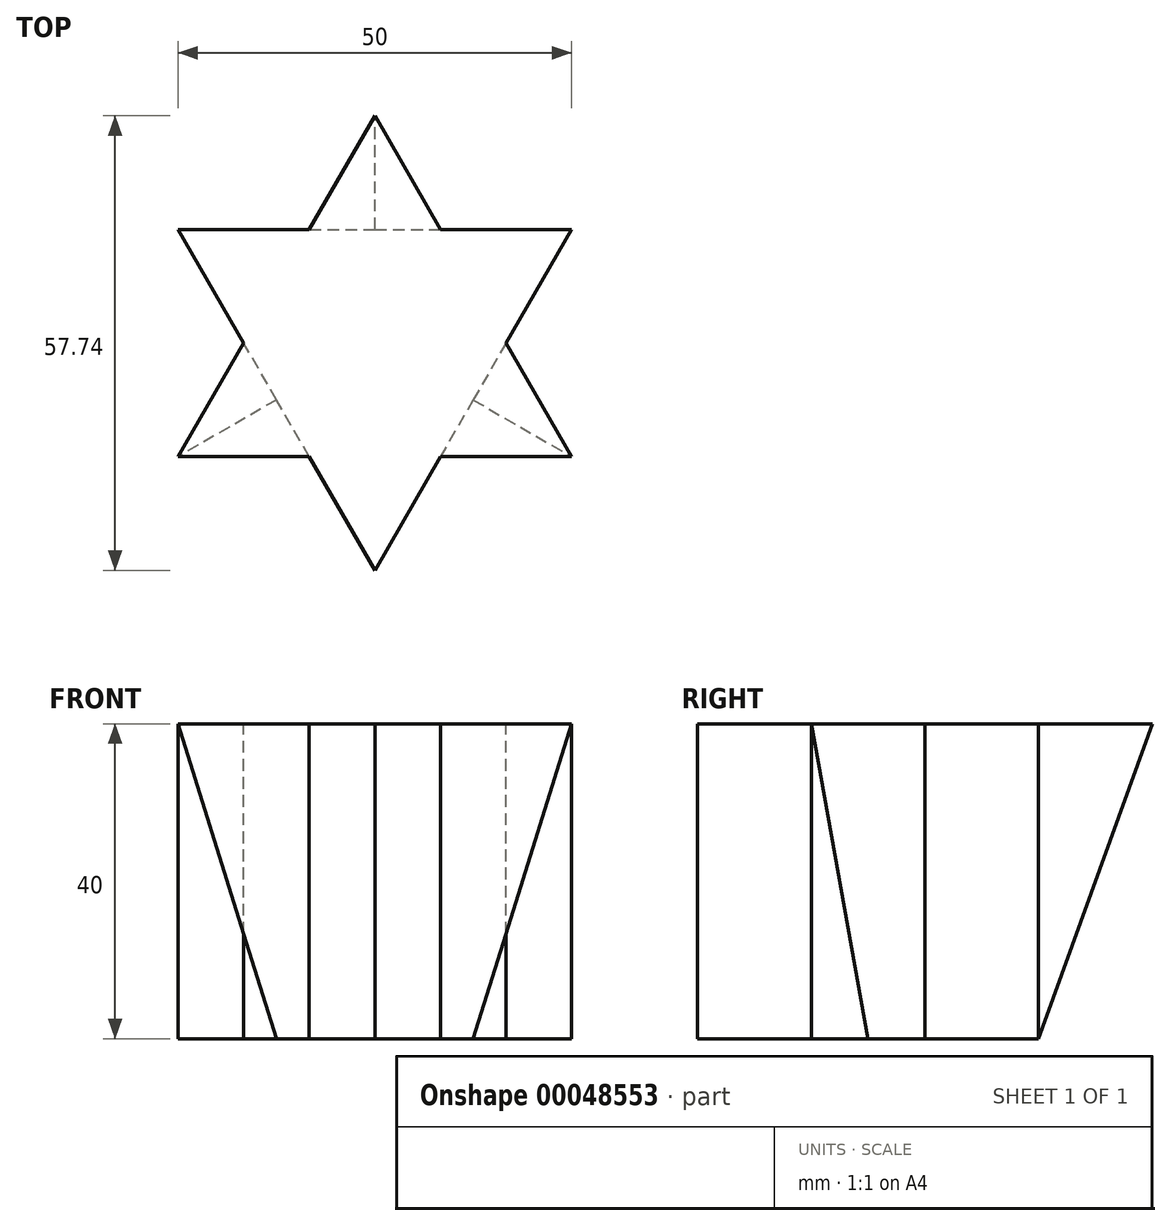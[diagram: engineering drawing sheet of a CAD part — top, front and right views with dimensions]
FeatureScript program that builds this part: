
annotation { "Feature Type Name" : "Feature", "Feature Type Description" : "" }
export const myFeature = defineFeature(function(context is Context, id is Id, definition is map)
    precondition{}
    {
        {
            var Q0;
            Q0=qCreatedBy(makeId("Top.planeOp"),FACE);
            var sketch = newSketch(context, id + "F0", { "sketchPlane" : qUnion([Q0])});
            skLineSegment(sketch, "E0.0", {"start": v(-25, 14.43) * mm, "end": v(-8.33, 14.43) * mm});
            skLineSegment(sketch, "E1", {"start": v(-8.33, 14.43) * mm, "end": v(8.33, 14.43) * mm});
            skLineSegment(sketch, "E2", {"start": v(8.33, 14.43) * mm, "end": v(25, 14.43) * mm});
            skLineSegment(sketch, "E3.1.0", {"start": v(0, -28.87) * mm, "end": v(-8.33, -14.43) * mm});
            skLineSegment(sketch, "E3.1.1", {"start": v(-16.67, 0) * mm, "end": v(-25, 14.43) * mm});
            skLineSegment(sketch, "E3.1.2", {"start": v(-8.33, -14.43) * mm, "end": v(-16.67, 0) * mm});
            skLineSegment(sketch, "E3.2.0", {"start": v(25, 14.43) * mm, "end": v(16.67, 0) * mm});
            skLineSegment(sketch, "E3.2.1", {"start": v(8.33, -14.43) * mm, "end": v(0, -28.87) * mm});
            skLineSegment(sketch, "E3.2.2", {"start": v(16.67, 0) * mm, "end": v(8.33, -14.43) * mm});
            skPoint(sketch, "E3.center", {"position": v(0, 0) * mm});
            skSolve(sketch);
        }
        {
            var Q0;
            Q0=qCreatedBy(makeId("Top.planeOp"),FACE);
            cPlane(context, id + "F1", {"entities" : qUnion([Q0]), "cplaneType" : CPlaneType.OFFSET, "offset" : 40 * mm, "width" : 150 * mm, "height" : 150 * mm});
        }
        {
            var Q0;
            Q0=qCreatedBy(id+"F1.planeOp",FACE);
            var sketch = newSketch(context, id + "F2", { "sketchPlane" : qUnion([Q0])});
            skLineSegment(sketch, "E4.0", {"start": v(-25, 14.43) * mm, "end": v(-8.33, 14.43) * mm});
            skPoint(sketch, "E4.0.midPoint", {"position": v(0, 14.43) * mm});
            skLineSegment(sketch, "E5", {"start": v(-8.33, 14.43) * mm, "end": v(0, 28.87) * mm});
            skLineSegment(sketch, "E6.MirrorCS", {"start": v(8.33, 14.43) * mm, "end": v(0, 28.87) * mm});
            skLineSegment(sketch, "E7.MirrorCS", {"start": v(25, 14.43) * mm, "end": v(8.33, 14.43) * mm});
            skLineSegment(sketch, "E8", {"start": v(-25, 14.43) * mm, "end": v(0, 0) * mm, "construction": true});
            skLineSegment(sketch, "E9.1.0", {"start": v(-16.67, 0) * mm, "end": v(-25, -14.43) * mm});
            skPoint(sketch, "E9.1.1", {"position": v(-12.5, -7.22) * mm});
            skLineSegment(sketch, "E9.1.2", {"start": v(-25, 14.43) * mm, "end": v(-16.67, 0) * mm});
            skLineSegment(sketch, "E9.1.3", {"start": v(0, -28.87) * mm, "end": v(-8.33, -14.43) * mm});
            skLineSegment(sketch, "E9.1.4", {"start": v(-8.33, -14.43) * mm, "end": v(-25, -14.43) * mm});
            skLineSegment(sketch, "E9.2.0", {"start": v(8.33, -14.43) * mm, "end": v(25, -14.43) * mm});
            skPoint(sketch, "E9.2.1", {"position": v(12.5, -7.22) * mm});
            skLineSegment(sketch, "E9.2.2", {"start": v(0, -28.87) * mm, "end": v(8.33, -14.43) * mm});
            skLineSegment(sketch, "E9.2.3", {"start": v(25, 14.43) * mm, "end": v(16.67, 0) * mm});
            skLineSegment(sketch, "E9.2.4", {"start": v(16.67, 0) * mm, "end": v(25, -14.43) * mm});
            skPoint(sketch, "E9.center", {"position": v(0, 0) * mm});
            skSolve(sketch);
        }
        {
            var Q0;
            Q0=qCreatedBy(id+"F1.planeOp",FACE);
            cPlane(context, id + "F3", {"entities" : qUnion([Q0]), "cplaneType" : CPlaneType.OFFSET, "offset" : 40 * mm, "width" : 150 * mm, "height" : 150 * mm});
        }
        {
            var Q0;
            Q0=makeQuery(id+"F0.imprint","IMPRINT",FACE,{"disambiguationData":[TD([[makeQuery(id+"F0.imprint","IMPRINT",EDGE,{"derivedFrom":sQuery(id+"F0.wireOp",EDGE,"E0.0")}),-1.0]])]});
            var Q1;
            Q1=makeQuery(id+"F2.imprint","IMPRINT",FACE,{"disambiguationData":[TD([[makeQuery(id+"F2.imprint","IMPRINT",EDGE,{"derivedFrom":sQuery(id+"F2.wireOp",EDGE,"E4.0")}),-1.0]])]});
            var Q2;
            Q2=sQuery(id+"F0.wireOp",VERTEX,"E3.2.1.end");
            var Q3;
            Q3=sQuery(id+"F2.wireOp",VERTEX,"E9.2.2.start");
            loft(context, id + "F4", {"sheetProfilesArray" : [{ "sheetProfileEntities" : qUnion([Q0]) }, { "sheetProfileEntities" : qUnion([Q1]) }], "matchConnections" : true, "connections" : [{ "connectionEntities" : qUnion([Q2, Q3]), "connectionEdgeQueries" : qUnion([]), "connectionEdgeParameters" : [] }]});
        }
    });
